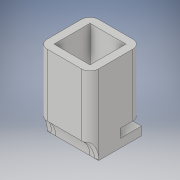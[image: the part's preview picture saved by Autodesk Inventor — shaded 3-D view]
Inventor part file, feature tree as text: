
AUTODESK INVENTOR PART (.ipt)
format: ipt  version: 2019.4 (Build 234330000, 330)  size: 192,000 bytes
history: native  units: mm
features: extrude x5, sketch x5, fillet x2
ambient origin geometry x8: Origin, YZ Plane, XZ Plane, XY Plane, X Axis, Y Axis, Z Axis, Center Point
bodies: Solid1 (feature_tree)
feature tree (12):
  extrude  "Extrusion1"  Depth=30.0mm
  extrude  "Extrusion2"  Depth=4.5mm
  extrude  "Extrusion3"  Depth=21.0mm
  fillet  "Fillet2"  Radius=21.0mm
  extrude  "Extrusion4"  Depth=15.0mm
  extrude  "Extrusion5"  Depth=13.0mm TaperAngle=0.0deg
  fillet  "Fillet3"  Radius=5.0mm
  sketch  "Sketch1"  dims[d0=30.0mm d1=30.0mm]
  sketch  "Sketch2"  dims[d2=36.35mm d3=0.0mm d4=4.5mm]
  sketch  "Sketch3"  dims[d5=4.5mm d6=21.0mm d7=21.0mm]
  sketch  "Sketch4"  dims[d8=30.0mm d9=0.0mm d10=15.0mm]
  sketch  "Sketch5"  dims[d11=4.0mm d12=5.0mm d13=0.0mm d15=5.0mm d16=10.0mm d17=6.0mm d18=90.0deg d19=60.0deg d20=5.0mm d21=0.0mm d22=30.0mm d23=25.0mm d24=5.0mm d25=0.0mm d26=13.0mm]
